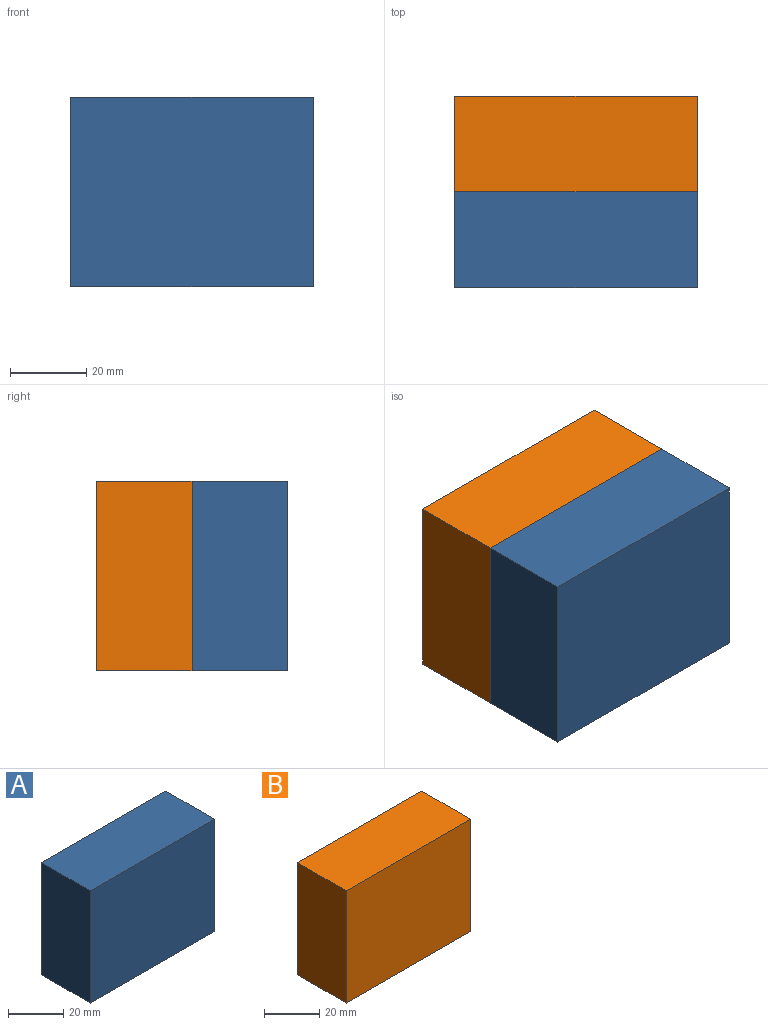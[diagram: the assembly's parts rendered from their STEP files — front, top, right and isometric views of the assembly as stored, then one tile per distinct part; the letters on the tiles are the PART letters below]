
ASSEMBLY  parts=2 mates=1
PART A: 6 faces, bbox 63.5x25x49.7 mm
  f0: plane 63.54x25mm, normal (0,0,1), area 1588.4mm2, adj f1,f3,f4,f5
  f1: plane 49.67x25mm, normal (-1,0,0), area 1241.8mm2, adj f0,f2,f4,f5
  f2: plane 63.54x25mm, normal (0,0,-1), area 1588.4mm2, adj f1,f3,f4,f5
  f3: plane 49.67x25mm, normal (1,0,0), area 1241.8mm2, adj f0,f2,f4,f5
  f4: plane 63.54x49.67mm, normal (0,-1,0), area 3156.2mm2, adj f0,f1,f2,f3
  f5: plane 63.54x49.67mm, normal (0,1,0), area 3156.2mm2, adj f0,f1,f2,f3
PART B: 6 faces, bbox 63.5x25x49.7 mm
  f0: plane 63.54x25mm, normal (0,0,1), area 1588.4mm2, adj f1,f3,f4,f5
  f1: plane 49.67x25mm, normal (-1,0,0), area 1241.8mm2, adj f0,f2,f4,f5
  f2: plane 63.54x25mm, normal (0,0,-1), area 1588.4mm2, adj f1,f3,f4,f5
  f3: plane 49.67x25mm, normal (1,0,0), area 1241.8mm2, adj f0,f2,f4,f5
  f4: plane 63.54x49.67mm, normal (0,-1,0), area 3156.2mm2, adj f0,f1,f2,f3
  f5: plane 63.54x49.67mm, normal (0,1,0), area 3156.2mm2, adj f0,f1,f2,f3
PLACE A t=(-27.07,67.22,-25.72)mm
PLACE B t=(-27.07,117.22,-25.72)mm
MATE revolute B.f4 <-> A.f5  axis (0,-1,0) through (-144.06,67.22,-0.89)mm
